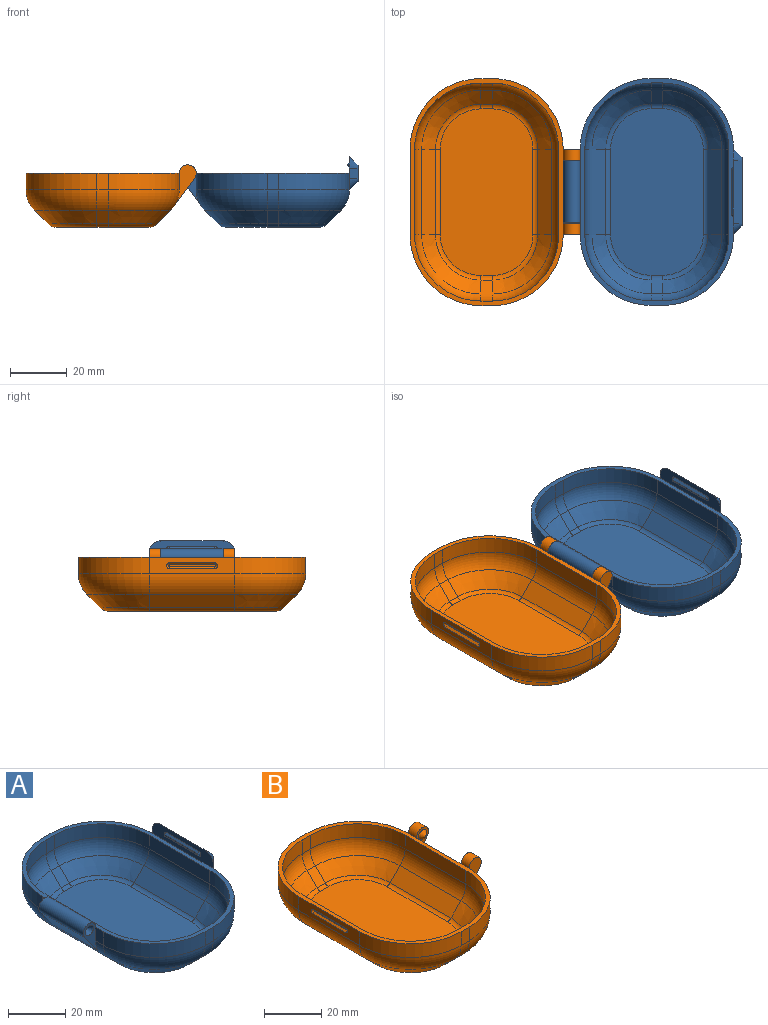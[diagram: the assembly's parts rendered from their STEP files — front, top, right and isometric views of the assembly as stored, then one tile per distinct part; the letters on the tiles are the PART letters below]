
ASSEMBLY  parts=2 mates=1
PART A: 92 faces, bbox 63x84.1x24.9 mm
  f0: plane 5.86x4.05mm, normal (-1,0,0), area 23.7mm2, adj f2,f8,f34,f86
  f1: plane 4x4mm, normal (1,0,0), area 3.4mm2, adj f9,f29,f72
  f2: plane 80x54mm, normal (0,0,1), area 352.1mm2, adj f0,f5,f6,f7,f8,f9,f10,f11
  f3: plane 58.69x32.69mm, normal (0,0,-1), area 1741.6mm2, adj f20,f21,f22,f23,f24,f25,f26,f27
  f4: plane 4x4mm, normal (1,0,0), area 3.4mm2, adj f11,f29,f76
  f5: plane 5.86x4.05mm, normal (-1,0,0), area 23.7mm2, adj f2,f10,f34,f89
  f6: plane 5.86x4mm, normal (0,-1,0), area 23.4mm2, adj f2,f10,f11,f30
  f7: plane 5.86x4mm, normal (0,1,0), area 23.4mm2, adj f2,f8,f9,f33
  f8: cylinder r=25mm len=25mm, axis (0,0,-1), area 230mm2, adj f0,f2,f7,f35
  f9: cylinder r=25mm len=25mm, axis (0,0,1), area 230mm2, adj f1,f2,f7,f31,f71
  f10: cylinder r=25mm len=25mm, axis (0,0,1), area 230mm2, adj f2,f5,f6,f32
  f11: cylinder r=25mm len=25mm, axis (0,0,-1), area 230mm2, adj f2,f4,f6,f28,f78
  f12: plane 30x4.9mm, normal (0.71,0,-0.71), area 207.9mm2, adj f13,f14,f22,f29
  f13: cone r=16mm half-angle=45deg, axis (0,0,1), area 213.6mm2, adj f12,f15,f20,f28
  f14: cone r=16mm half-angle=45deg, axis (0,0,1), area 213.6mm2, adj f12,f16,f24,f31
  f15: plane 4.9x4.9mm, normal (0,-0.71,-0.71), area 27.7mm2, adj f13,f17,f21,f30
  f16: plane 4.9x4.9mm, normal (0,0.71,-0.71), area 27.7mm2, adj f14,f18,f26,f33
  f17: cone r=16mm half-angle=45deg, axis (0,0,1), area 213.6mm2, adj f15,f19,f23,f32
  f18: cone r=16mm half-angle=45deg, axis (0,0,1), area 213.6mm2, adj f16,f19,f27,f35
  f19: plane 30x4.9mm, normal (-0.71,0,-0.71), area 207.9mm2, adj f17,f18,f25,f34
  f20: torus R=14.34mm, axis (0,0,-1), area 78.1mm2, adj f3,f13,f21,f22
  f21: cylinder r=4mm len=4mm, axis (1,0,0), area 12.6mm2, adj f3,f15,f20,f23
  f22: cylinder r=4mm len=30mm, axis (0,1,0), area 94.2mm2, adj f3,f12,f20,f24
  f23: torus R=14.34mm, axis (0,0,-1), area 78.1mm2, adj f3,f17,f21,f25
  f24: torus R=14.34mm, axis (0,0,-1), area 78.1mm2, adj f3,f14,f22,f26
  f25: cylinder r=4mm len=30mm, axis (0,1,0), area 94.2mm2, adj f3,f19,f23,f27
  f26: cylinder r=4mm len=4mm, axis (1,0,0), area 12.6mm2, adj f3,f16,f24,f27
  f27: torus R=14.34mm, axis (0,0,-1), area 78.1mm2, adj f3,f18,f25,f26
  f28: torus R=15mm, axis (0,0,-1), area 296.1mm2, adj f11,f13,f29,f30
  f29: cylinder r=10mm len=30mm, axis (0,-1,0), area 235.6mm2, adj f1,f4,f12,f28,f31,f74
  f30: cylinder r=10mm len=7.07mm, axis (-1,0,0), area 31.4mm2, adj f6,f15,f28,f32
  f31: torus R=15mm, axis (0,0,-1), area 296.1mm2, adj f9,f14,f29,f33
  f32: torus R=15mm, axis (0,0,-1), area 296.1mm2, adj f10,f17,f30,f34
  f33: cylinder r=10mm len=7.07mm, axis (1,0,0), area 31.4mm2, adj f7,f16,f31,f35
  f34: cylinder r=10mm len=30mm, axis (0,1,0), area 126.2mm2, adj f0,f5,f19,f32,f35,f86,f89,f91
  f35: torus R=15mm, axis (0,0,-1), area 296.1mm2, adj f8,f18,f33,f34
  f36: plane 58.69x32.69mm, normal (0,0,1), area 1741.6mm2, adj f53,f54,f55,f56,f57,f58,f59,f60
  f37: plane 30x5.86mm, normal (-1,0,0), area 175.7mm2, adj f2,f42,f44,f62
  f38: plane 30x5.86mm, normal (1,0,0), area 175.7mm2, adj f2,f41,f43,f67
  f39: plane 5.86x4mm, normal (0,1,0), area 23.4mm2, adj f2,f43,f44,f63
  f40: plane 5.86x4mm, normal (0,-1,0), area 23.4mm2, adj f2,f41,f42,f66
  f41: cylinder r=23.4mm len=23.4mm, axis (0,0,-1), area 215.3mm2, adj f2,f38,f40,f68
  f42: cylinder r=23.4mm len=23.4mm, axis (0,0,1), area 215.3mm2, adj f2,f37,f40,f64
  f43: cylinder r=23.4mm len=23.4mm, axis (0,0,1), area 215.3mm2, adj f2,f38,f39,f65
  f44: cylinder r=23.4mm len=23.4mm, axis (0,0,-1), area 215.3mm2, adj f2,f37,f39,f61
  f45: plane 30x4.9mm, normal (-0.71,0,0.71), area 207.9mm2, adj f46,f47,f55,f62
  f46: cone r=14.87mm half-angle=45deg, axis (0,0,1), area 201.2mm2, adj f45,f48,f53,f61
  f47: cone r=14.87mm half-angle=45deg, axis (0,0,1), area 201.2mm2, adj f45,f49,f57,f64
  f48: plane 4.9x4.9mm, normal (0,0.71,0.71), area 27.7mm2, adj f46,f50,f54,f63
  f49: plane 4.9x4.9mm, normal (0,-0.71,0.71), area 27.7mm2, adj f47,f51,f59,f66
  f50: cone r=14.87mm half-angle=45deg, axis (0,0,1), area 201.2mm2, adj f48,f52,f56,f65
  f51: cone r=14.87mm half-angle=45deg, axis (0,0,1), area 201.2mm2, adj f49,f52,f60,f68
  f52: plane 30x4.9mm, normal (0.71,0,0.71), area 207.9mm2, adj f50,f51,f58,f67
  f53: torus R=14.34mm, axis (0,0,-1), area 45.1mm2, adj f36,f46,f54,f55
  f54: cylinder r=2.4mm len=4mm, axis (1,0,0), area 7.5mm2, adj f36,f48,f53,f56
  f55: cylinder r=2.4mm len=30mm, axis (0,1,0), area 56.5mm2, adj f36,f45,f53,f57
  f56: torus R=14.34mm, axis (0,0,-1), area 45.1mm2, adj f36,f50,f54,f58
  f57: torus R=14.34mm, axis (0,0,-1), area 45.1mm2, adj f36,f47,f55,f59
  f58: cylinder r=2.4mm len=30mm, axis (0,1,0), area 56.5mm2, adj f36,f52,f56,f60
  f59: cylinder r=2.4mm len=4mm, axis (1,0,0), area 7.5mm2, adj f36,f49,f57,f60
  f60: torus R=14.34mm, axis (0,0,-1), area 45.1mm2, adj f36,f51,f58,f59
  f61: torus R=15mm, axis (0,0,-1), area 233.8mm2, adj f44,f46,f62,f63
  f62: cylinder r=8.4mm len=30mm, axis (0,-1,0), area 197.9mm2, adj f37,f45,f61,f64
  f63: cylinder r=8.4mm len=5.94mm, axis (-1,0,0), area 26.4mm2, adj f39,f48,f61,f65
  f64: torus R=15mm, axis (0,0,-1), area 233.8mm2, adj f42,f47,f62,f66
  f65: torus R=15mm, axis (0,0,-1), area 233.8mm2, adj f43,f50,f63,f67
  f66: cylinder r=8.4mm len=5.94mm, axis (1,0,0), area 26.4mm2, adj f40,f49,f64,f68
  f67: cylinder r=8.4mm len=30mm, axis (0,1,0), area 197.9mm2, adj f38,f52,f65,f68
  f68: torus R=15mm, axis (0,0,-1), area 233.8mm2, adj f41,f51,f66,f67
  f69: plane 30x5.86mm, normal (-1,0,0), area 133.7mm2, adj f2,f71,f73,f75,f77,f78,f80,f81
  f70: plane 24x5.72mm, normal (1,0,0), area 136.3mm2, adj f71,f72,f73,f74,f75,f76,f77,f78
  f71: plane 3.72x3mm, normal (0.71,0.71,0), area 15.8mm2, adj f9,f69,f70,f72,f73
  f72: cone r=1mm half-angle=45deg, axis (-1,0,0), area 16.7mm2, adj f1,f70,f71,f74
  f73: cone r=1mm half-angle=45deg, axis (-1,0,0), area 16.7mm2, adj f69,f70,f71,f75
  f74: plane 22x3mm, normal (0.71,0,-0.71), area 93.3mm2, adj f29,f70,f72,f76
  f75: plane 22x3mm, normal (0.71,0,0.71), area 93.3mm2, adj f69,f70,f73,f77
  f76: cone r=1mm half-angle=45deg, axis (-1,0,0), area 16.7mm2, adj f4,f70,f74,f78
  f77: cone r=1mm half-angle=45deg, axis (-1,0,0), area 16.7mm2, adj f69,f70,f75,f78
  f78: plane 3.72x3mm, normal (0.71,-0.71,0), area 15.8mm2, adj f11,f69,f70,f76,f77
  f79: plane 16.5x0.5mm, normal (-1,0,0), area 8.2mm2, adj f80,f81,f82,f83
  f80: plane 16x0.75mm, normal (-0.71,0,0.71), area 17mm2, adj f69,f79,f81,f82
  f81: cone r=0.25mm half-angle=45deg, axis (1,0,0), area 2.1mm2, adj f69,f79,f80,f83
  f82: cone r=0.25mm half-angle=45deg, axis (1,0,0), area 2.1mm2, adj f69,f79,f80,f83
  f83: plane 16x0.75mm, normal (-0.71,0,-0.71), area 17mm2, adj f69,f79,f81,f82
  f84: cylinder r=3mm len=21.9mm, axis (0,1,0), area 248.6mm2, adj f2,f86,f89,f91
  f85: cone r=2mm half-angle=45deg, axis (0,1,0), area 17.4mm2, adj f86,f87
  f86: plane 13.65x7.22mm, normal (0,1,0), area 32.4mm2, adj f0,f34,f84,f85,f91
  f87: plane 0.6x0.6mm, normal (0,1,0), area 0.3mm2, adj f85
  f88: cone r=2mm half-angle=45deg, axis (0,-1,0), area 17.4mm2, adj f89,f90
  f89: plane 13.65x7.22mm, normal (0,-1,0), area 32.4mm2, adj f5,f34,f84,f88,f91
  f90: plane 0.6x0.6mm, normal (0,-1,0), area 0.3mm2, adj f88
  f91: plane 21.9x8.85mm, normal (-0.8,0,-0.6), area 242.1mm2, adj f34,f84,f86,f89
PART B: 88 faces, bbox 62.1x84.1x22 mm
  f0: plane 22x5.86mm, normal (1,0,0), area 128.9mm2, adj f1,f2,f77,f82
  f1: cylinder r=10mm len=30mm, axis (0,1,0), area 184.9mm2, adj f0,f13,f23,f25,f77,f81,f82,f87
  f2: plane 80x54mm, normal (0,0,1), area 352.1mm2, adj f0,f27,f28,f29,f30,f31,f32,f33
  f3: plane 58.69x32.69mm, normal (0,0,-1), area 1741.6mm2, adj f4,f5,f6,f7,f8,f9,f10,f11
  f4: cylinder r=4mm len=30mm, axis (0,1,0), area 94.2mm2, adj f3,f9,f11,f12
  f5: cylinder r=4mm len=30mm, axis (0,1,0), area 94.2mm2, adj f3,f8,f10,f13
  f6: cylinder r=4mm len=4mm, axis (-1,0,0), area 12.6mm2, adj f3,f10,f11,f14
  f7: cylinder r=4mm len=4mm, axis (-1,0,0), area 12.6mm2, adj f3,f8,f9,f15
  f8: torus R=14.34mm, axis (0,0,-1), area 78.1mm2, adj f3,f5,f7,f16
  f9: torus R=14.34mm, axis (0,0,-1), area 78.1mm2, adj f3,f4,f7,f17
  f10: torus R=14.34mm, axis (0,0,-1), area 78.1mm2, adj f3,f5,f6,f18
  f11: torus R=14.34mm, axis (0,0,-1), area 78.1mm2, adj f3,f4,f6,f19
  f12: plane 30x4.9mm, normal (-0.71,0,-0.71), area 207.9mm2, adj f4,f17,f19,f20
  f13: plane 30x4.9mm, normal (0.71,0,-0.71), area 207.9mm2, adj f1,f5,f16,f18
  f14: plane 4.9x4.9mm, normal (0,-0.71,-0.71), area 27.7mm2, adj f6,f18,f19,f21
  f15: plane 4.9x4.9mm, normal (0,0.71,-0.71), area 27.7mm2, adj f7,f16,f17,f22
  f16: cone r=16mm half-angle=45deg, axis (0,0,1), area 213.6mm2, adj f8,f13,f15,f23
  f17: cone r=16mm half-angle=45deg, axis (0,0,1), area 213.6mm2, adj f9,f12,f15,f24
  f18: cone r=16mm half-angle=45deg, axis (0,0,1), area 213.6mm2, adj f10,f13,f14,f25
  f19: cone r=16mm half-angle=45deg, axis (0,0,1), area 213.6mm2, adj f11,f12,f14,f26
  f20: cylinder r=10mm len=30mm, axis (0,-1,0), area 235.6mm2, adj f12,f24,f26,f33
  f21: cylinder r=10mm len=7.07mm, axis (1,0,0), area 31.4mm2, adj f14,f25,f26,f32
  f22: cylinder r=10mm len=7.07mm, axis (-1,0,0), area 31.4mm2, adj f15,f23,f24,f29
  f23: torus R=15mm, axis (0,0,-1), area 296.1mm2, adj f1,f16,f22,f28,f85
  f24: torus R=15mm, axis (0,0,-1), area 296.1mm2, adj f17,f20,f22,f27
  f25: torus R=15mm, axis (0,0,-1), area 296.1mm2, adj f1,f18,f21,f31,f80
  f26: torus R=15mm, axis (0,0,-1), area 296.1mm2, adj f19,f20,f21,f30
  f27: cylinder r=25mm len=25mm, axis (0,0,-1), area 230mm2, adj f2,f24,f29,f33
  f28: cylinder r=25mm len=25mm, axis (0,0,1), area 230mm2, adj f2,f23,f29,f85
  f29: plane 5.86x4mm, normal (0,1,0), area 23.4mm2, adj f2,f22,f27,f28
  f30: cylinder r=25mm len=25mm, axis (0,0,1), area 230mm2, adj f2,f26,f32,f33
  f31: cylinder r=25mm len=25mm, axis (0,0,-1), area 230mm2, adj f2,f25,f32,f80
  f32: plane 5.86x4mm, normal (0,-1,0), area 23.4mm2, adj f2,f21,f30,f31
  f33: plane 30x5.86mm, normal (-1,0,0), area 140.6mm2, adj f2,f20,f27,f30,f67,f68,f69,f70
  f34: plane 58.69x32.69mm, normal (0,0,1), area 1741.6mm2, adj f35,f36,f37,f38,f39,f40,f41,f42
  f35: cylinder r=2.4mm len=30mm, axis (0,1,0), area 56.5mm2, adj f34,f40,f42,f43
  f36: cylinder r=2.4mm len=30mm, axis (0,1,0), area 56.5mm2, adj f34,f39,f41,f44
  f37: cylinder r=2.4mm len=4mm, axis (-1,0,0), area 7.5mm2, adj f34,f41,f42,f45
  f38: cylinder r=2.4mm len=4mm, axis (-1,0,0), area 7.5mm2, adj f34,f39,f40,f46
  f39: torus R=14.34mm, axis (0,0,-1), area 45.1mm2, adj f34,f36,f38,f47
  f40: torus R=14.34mm, axis (0,0,-1), area 45.1mm2, adj f34,f35,f38,f48
  f41: torus R=14.34mm, axis (0,0,-1), area 45.1mm2, adj f34,f36,f37,f49
  f42: torus R=14.34mm, axis (0,0,-1), area 45.1mm2, adj f34,f35,f37,f50
  f43: plane 30x4.9mm, normal (0.71,0,0.71), area 207.9mm2, adj f35,f48,f50,f51
  f44: plane 30x4.9mm, normal (-0.71,0,0.71), area 207.9mm2, adj f36,f47,f49,f52
  f45: plane 4.9x4.9mm, normal (0,0.71,0.71), area 27.7mm2, adj f37,f49,f50,f53
  f46: plane 4.9x4.9mm, normal (0,-0.71,0.71), area 27.7mm2, adj f38,f47,f48,f54
  f47: cone r=14.87mm half-angle=45deg, axis (0,0,1), area 201.2mm2, adj f39,f44,f46,f55
  f48: cone r=14.87mm half-angle=45deg, axis (0,0,1), area 201.2mm2, adj f40,f43,f46,f56
  f49: cone r=14.87mm half-angle=45deg, axis (0,0,1), area 201.2mm2, adj f41,f44,f45,f57
  f50: cone r=14.87mm half-angle=45deg, axis (0,0,1), area 201.2mm2, adj f42,f43,f45,f58
  f51: cylinder r=8.4mm len=30mm, axis (0,-1,0), area 197.9mm2, adj f43,f56,f58,f66
  f52: cylinder r=8.4mm len=30mm, axis (0,1,0), area 197.9mm2, adj f44,f55,f57,f65
  f53: cylinder r=8.4mm len=5.94mm, axis (1,0,0), area 26.4mm2, adj f45,f57,f58,f64
  f54: cylinder r=8.4mm len=5.94mm, axis (-1,0,0), area 26.4mm2, adj f46,f55,f56,f61
  f55: torus R=15mm, axis (0,0,-1), area 233.8mm2, adj f47,f52,f54,f60
  f56: torus R=15mm, axis (0,0,-1), area 233.8mm2, adj f48,f51,f54,f59
  f57: torus R=15mm, axis (0,0,-1), area 233.8mm2, adj f49,f52,f53,f63
  f58: torus R=15mm, axis (0,0,-1), area 233.8mm2, adj f50,f51,f53,f62
  f59: cylinder r=23.4mm len=23.4mm, axis (0,0,-1), area 215.3mm2, adj f2,f56,f61,f66
  f60: cylinder r=23.4mm len=23.4mm, axis (0,0,1), area 215.3mm2, adj f2,f55,f61,f65
  f61: plane 5.86x4mm, normal (0,-1,0), area 23.4mm2, adj f2,f54,f59,f60
  f62: cylinder r=23.4mm len=23.4mm, axis (0,0,1), area 215.3mm2, adj f2,f58,f64,f66
  f63: cylinder r=23.4mm len=23.4mm, axis (0,0,-1), area 215.3mm2, adj f2,f57,f64,f65
  f64: plane 5.86x4mm, normal (0,1,0), area 23.4mm2, adj f2,f53,f62,f63
  f65: plane 30x5.86mm, normal (-1,0,0), area 175.7mm2, adj f2,f52,f60,f63
  f66: plane 30x5.86mm, normal (1,0,0), area 175.7mm2, adj f2,f51,f59,f62
  f67: cone r=1mm half-angle=45deg, axis (1,0,0), area 0mm2, adj f33,f68,f70,f72
  f68: plane 16x0mm, normal (0.71,0,0.71), area 0mm2, adj f33,f67,f69,f73
  f69: cone r=1mm half-angle=45deg, axis (1,0,0), area 0mm2, adj f33,f68,f70,f71
  f70: plane 16x0mm, normal (0.71,0,-0.71), area 0mm2, adj f33,f67,f69,f75
  f71: cone r=0.25mm half-angle=45deg, axis (-1,0,0), area 2.1mm2, adj f69,f73,f74,f75
  f72: cone r=0.25mm half-angle=45deg, axis (-1,0,0), area 2.1mm2, adj f67,f73,f74,f75
  f73: plane 16x0.75mm, normal (-0.71,0,0.71), area 17mm2, adj f68,f71,f72,f74
  f74: plane 16.5x0.5mm, normal (-1,0,0), area 8.2mm2, adj f71,f72,f73,f75
  f75: plane 16x0.75mm, normal (-0.71,0,-0.71), area 17mm2, adj f70,f71,f72,f74
  f76: cylinder r=3mm len=6mm, axis (0,-1,0), area 45.3mm2, adj f2,f77,f80,f81
  f77: plane 14.78x7.95mm, normal (0,1,0), area 33mm2, adj f0,f1,f76,f78,f81
  f78: cone r=2mm half-angle=45deg, axis (0,-1,0), area 17.4mm2, adj f77,f79
  f79: plane 0.6x0.6mm, normal (0,1,0), area 0.3mm2, adj f78
  f80: plane 14.78x7.95mm, normal (0,-1,0), area 45.5mm2, adj f25,f31,f76,f81
  f81: plane 10.01x7.36mm, normal (0.81,0,-0.59), area 49.7mm2, adj f1,f76,f77,f80
  f82: plane 14.78x7.95mm, normal (0,-1,0), area 33mm2, adj f0,f1,f83,f86,f87
  f83: cone r=2mm half-angle=45deg, axis (0,1,0), area 17.4mm2, adj f82,f84
  f84: plane 0.6x0.6mm, normal (0,-1,0), area 0.3mm2, adj f83
  f85: plane 14.78x7.95mm, normal (0,1,0), area 45.5mm2, adj f23,f28,f86,f87
  f86: cylinder r=3mm len=6mm, axis (0,1,0), area 45.3mm2, adj f2,f82,f85,f87
  f87: plane 10.01x7.36mm, normal (0.81,0,-0.59), area 49.7mm2, adj f1,f82,f85,f86
PLACE A t=(-44.56,-15.95,8.42)mm
PLACE B t=(-44.56,-16,8.42)mm
MATE revolute A.f84 <-> B.f76  axis (0,1,0) through (-14.56,-6.7,8.42)mm
